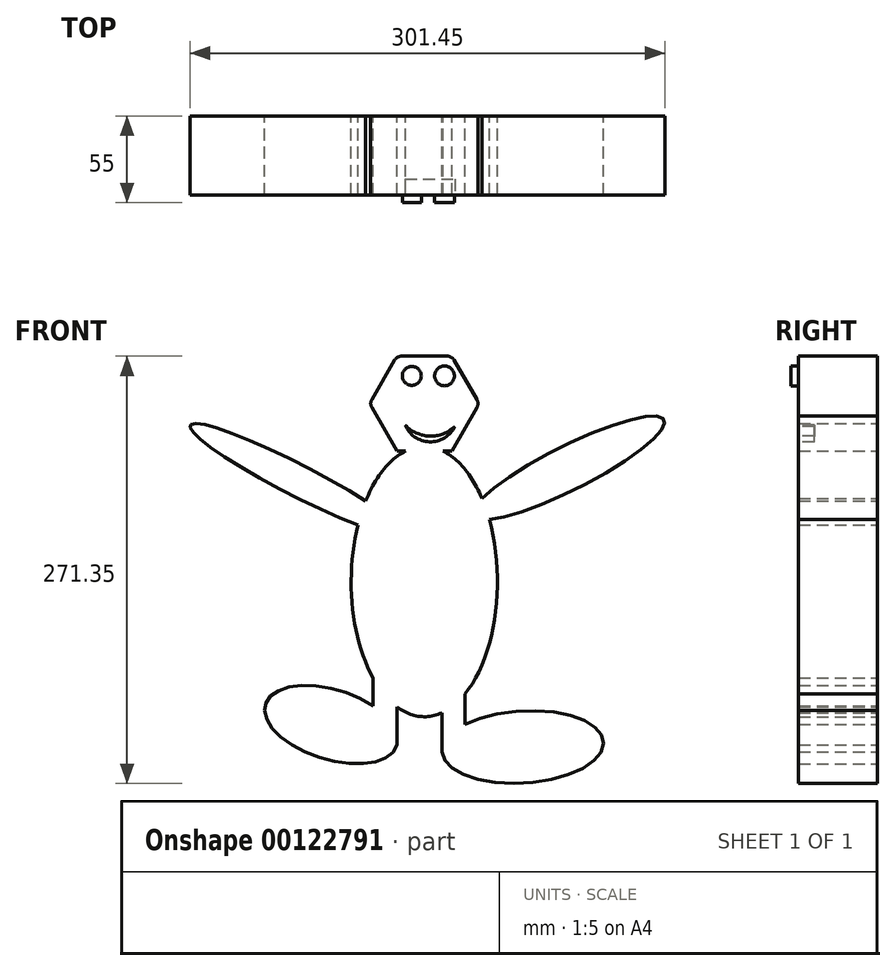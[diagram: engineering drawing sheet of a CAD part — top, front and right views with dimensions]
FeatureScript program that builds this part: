
annotation { "Feature Type Name" : "Feature", "Feature Type Description" : "" }
export const myFeature = defineFeature(function(context is Context, id is Id, definition is map)
    precondition{}
    {
        {
            var Q0;
            Q0=qCreatedBy(makeId("Front.planeOp"),FACE);
            var sketch = newSketch(context, id + "F0", { "sketchPlane" : qUnion([Q0])});
            skCircle(sketch, "E0.cCircle", {"center": v(0, 0) * mm, "radius": 30.16 * mm, "construction": true});
            skLineSegment(sketch, "E0.0", {"start": v(-17.41, 30.16) * mm, "end": v(17.41, 30.16) * mm});
            skLineSegment(sketch, "E0.1", {"start": v(17.41, 30.16) * mm, "end": v(34.83, 0) * mm});
            skLineSegment(sketch, "E0.2", {"start": v(34.83, 0) * mm, "end": v(17.41, -30.16) * mm});
            skLineSegment(sketch, "E0.3", {"start": v(17.41, -30.16) * mm, "end": v(-17.41, -30.16) * mm});
            skLineSegment(sketch, "E0.4", {"start": v(-17.41, -30.16) * mm, "end": v(-34.83, 0) * mm});
            skLineSegment(sketch, "E0.5", {"start": v(-34.83, 0) * mm, "end": v(-17.41, 30.16) * mm});
            skPoint(sketch, "E0.0.midPoint", {"position": v(0, 30.16) * mm});
            skSolve(sketch);
        }
        {
            var Q0;
            Q0=makeQuery(id+"F0.imprint","IMPRINT",FACE,{"disambiguationData":[TD([[makeQuery(id+"F0.imprint","IMPRINT",EDGE,{"derivedFrom":sQuery(id+"F0.wireOp",EDGE,"E0.0")}),-1.0]])]});
            extrude(context, id + "F1", {"entities" : qUnion([Q0]), "depth" : 50 * mm});
        }
        {
            var Q0;
            Q0=makeQuery(id+"F1.opExtrude","CAP_FACE",FACE,{"disambiguationData":[OSD([sQuery(id+"F0.wireOp",EDGE,"E0.0"),sQuery(id+"F0.wireOp",EDGE,"E0.1"),sQuery(id+"F0.wireOp",EDGE,"E0.2"),sQuery(id+"F0.wireOp",EDGE,"E0.3"),sQuery(id+"F0.wireOp",EDGE,"E0.4"),sQuery(id+"F0.wireOp",EDGE,"E0.5")])],"isStart":false});
            var sketch = newSketch(context, id + "F2", { "sketchPlane" : qUnion([Q0])});
            skCircle(sketch, "E1", {"center": v(12.81, 17.63) * mm, "radius": 6.28 * mm});
            skCircle(sketch, "E2", {"center": v(-7.97, 17.63) * mm, "radius": 6.02 * mm});
            skArc(sketch, "E3", {"start": v(-12.24, -13.47) * mm, "mid": v(3.23, -24.2) * mm, "end": v(19.33, -14.44) * mm});
            skArc(sketch, "E4", {"start": v(-12.24, -13.47) * mm, "mid": v(3.34, -20.6) * mm, "end": v(19.33, -14.44) * mm});
            skSolve(sketch);
        }
        {
            var Q0;
            Q0=makeQuery(id+"F2.imprint","IMPRINT",FACE,{"disambiguationData":[TD([[makeQuery(id+"F2.imprint","IMPRINT",EDGE,{"derivedFrom":sQuery(id+"F2.wireOp",EDGE,"E2")}),1.0]])]});
            var Q1;
            Q1=makeQuery(id+"F2.imprint","IMPRINT",FACE,{"disambiguationData":[TD([[makeQuery(id+"F2.imprint","IMPRINT",EDGE,{"derivedFrom":sQuery(id+"F2.wireOp",EDGE,"E1")}),1.0]])]});
            extrude(context, id + "F3", {"entities" : qUnion([Q0, Q1]), "operationType" : NewBodyOperationType.ADD, "depth" : 5 * mm});
        }
        {
            var Q0;
            Q0=makeQuery(id+"F2.imprint","IMPRINT",FACE,{"disambiguationData":[TD([[makeQuery(id+"F2.imprint","IMPRINT",EDGE,{"derivedFrom":sQuery(id+"F2.wireOp",EDGE,"E3")}),1.0]])]});
            extrude(context, id + "F4", {"entities" : qUnion([Q0]), "operationType" : NewBodyOperationType.REMOVE, "oppositeDirection" : true, "depth" : 10 * mm});
        }
        {
            var Q0;
            Q0=makeQuery(id+"F1.opExtrude","SWEPT_EDGE",EDGE,{"disambiguationData":[OSD([sQuery(id+"F0.wireOp",EDGE,"E0.0"),sQuery(id+"F0.wireOp",EDGE,"E0.1")])]});
            var Q1;
            Q1=makeQuery(id+"F1.opExtrude","SWEPT_EDGE",EDGE,{"disambiguationData":[OSD([sQuery(id+"F0.wireOp",EDGE,"E0.0"),sQuery(id+"F0.wireOp",EDGE,"E0.5")])]});
            var Q2;
            Q2=makeQuery(id+"F1.opExtrude","SWEPT_EDGE",EDGE,{"disambiguationData":[OSD([sQuery(id+"F0.wireOp",EDGE,"E0.1"),sQuery(id+"F0.wireOp",EDGE,"E0.2")])]});
            var Q3;
            Q3=makeQuery(id+"F1.opExtrude","SWEPT_EDGE",EDGE,{"disambiguationData":[OSD([sQuery(id+"F0.wireOp",EDGE,"E0.4"),sQuery(id+"F0.wireOp",EDGE,"E0.5")])]});
            fillet(context, id + "F5", {"entities" : qUnion([Q0, Q1, Q2, Q3]), "radius" : 5 * mm, "tangentPropagation" : true, "allowEdgeOverflow" : false});
        }
        {
            var Q0;
            Q0=qCreatedBy(makeId("Front.planeOp"),FACE);
            var sketch = newSketch(context, id + "F6", { "sketchPlane" : qUnion([Q0])});
            skEllipse(sketch, "E5", {"center": v(0, -113.06) * mm, "majorRadius": 85.77 * mm, "minorRadius": 46.48 * mm, "majorAxis": v(0, 1)});
            skLineSegment(sketch, "E6.bottom", {"start": v(25.73, -221.24) * mm, "end": v(11.2, -221.24) * mm});
            skLineSegment(sketch, "E6.top", {"start": v(25.73, -181.67) * mm, "end": v(11.2, -181.67) * mm});
            skLineSegment(sketch, "E6.left", {"start": v(25.73, -221.24) * mm, "end": v(25.73, -181.67) * mm});
            skLineSegment(sketch, "E6.right", {"start": v(11.2, -221.24) * mm, "end": v(11.2, -181.67) * mm});
            skLineSegment(sketch, "E7.bottom", {"start": v(-32.66, -216.9) * mm, "end": v(-17.43, -216.9) * mm});
            skLineSegment(sketch, "E7.top", {"start": v(-32.66, -169.58) * mm, "end": v(-17.43, -169.58) * mm});
            skLineSegment(sketch, "E7.left", {"start": v(-32.66, -216.9) * mm, "end": v(-32.66, -169.58) * mm});
            skLineSegment(sketch, "E7.right", {"start": v(-17.43, -216.9) * mm, "end": v(-17.43, -169.58) * mm});
            skEllipse(sketch, "E8", {"center": v(62.55, -218.08) * mm, "majorRadius": 51.44 * mm, "minorRadius": 22.94 * mm, "majorAxis": v(-1, -0.06)});
            skEllipse(sketch, "E9", {"center": v(-59.15, -203.88) * mm, "majorRadius": 43.7 * mm, "minorRadius": 22.25 * mm, "majorAxis": v(0.95, -0.3)});
            skEllipse(sketch, "E10", {"center": v(91.5, -40.9) * mm, "majorRadius": 68.1 * mm, "minorRadius": 13.96 * mm, "majorAxis": v(-0.9, -0.45)});
            skEllipse(sketch, "E11", {"center": v(-81.37, -48.27) * mm, "majorRadius": 75.6 * mm, "minorRadius": 10.05 * mm, "majorAxis": v(0.89, -0.46)});
            skSolve(sketch);
        }
        {
            var Q0;
            {var subQ0=sQuery(id+"F6.wireOp",EDGE,"E10");var subQ1=sQuery(id+"F6.wireOp",EDGE,"E5");var subQ2=makeQuery(id+"F6.imprint","INTERSECT",VERTEX,{"disambiguationData":[OD(0.0)],"derivedFrom":[subQ1,subQ0]});Q0=makeQuery(id+"F6.imprint","IMPRINT",FACE,{"disambiguationData":[TD([[makeQuery(id+"F6.imprint","IMPRINT",EDGE,{"disambiguationData":[TD([[subQ2,-1.0]])],"derivedFrom":subQ1}),-1.0]])]});}
            var Q1;
            {var subQ0=sQuery(id+"F6.wireOp",EDGE,"E11");var subQ1=sQuery(id+"F6.wireOp",EDGE,"E5");var subQ2=makeQuery(id+"F6.imprint","INTERSECT",VERTEX,{"disambiguationData":[OD(0.0)],"derivedFrom":[subQ1,subQ0]});Q1=makeQuery(id+"F6.imprint","IMPRINT",FACE,{"disambiguationData":[TD([[makeQuery(id+"F6.imprint","IMPRINT",EDGE,{"disambiguationData":[TD([[subQ2,1.0]])],"derivedFrom":subQ1}),-1.0]])]});}
            var Q2;
            {var subQ7=sQuery(id+"F6.wireOp",EDGE,"E6.top");Q2=makeQuery(id+"F6.imprint","IMPRINT",FACE,{"disambiguationData":[TD([[makeQuery(id+"F6.imprint","IMPRINT",EDGE,{"derivedFrom":subQ7}),-1.0]])]});}
            var Q3;
            {var subQ0=sQuery(id+"F6.wireOp",EDGE,"E10");var subQ1=sQuery(id+"F6.wireOp",EDGE,"E5");var subQ2=makeQuery(id+"F6.imprint","INTERSECT",VERTEX,{"disambiguationData":[OD(0.0)],"derivedFrom":[subQ1,subQ0]});Q3=makeQuery(id+"F6.imprint","IMPRINT",FACE,{"disambiguationData":[TD([[makeQuery(id+"F6.imprint","IMPRINT",EDGE,{"disambiguationData":[TD([[subQ2,-1.0]])],"derivedFrom":subQ1}),1.0]])]});}
            var Q4;
            {var subQ0=sQuery(id+"F6.wireOp",EDGE,"E11");var subQ1=sQuery(id+"F6.wireOp",EDGE,"E5");var subQ2=makeQuery(id+"F6.imprint","INTERSECT",VERTEX,{"disambiguationData":[OD(0.0)],"derivedFrom":[subQ1,subQ0]});Q4=makeQuery(id+"F6.imprint","IMPRINT",FACE,{"disambiguationData":[TD([[makeQuery(id+"F6.imprint","IMPRINT",EDGE,{"disambiguationData":[TD([[subQ2,1.0]])],"derivedFrom":subQ1}),1.0]])]});}
            var Q5;
            {var subQ5=sQuery(id+"F6.wireOp",EDGE,"E7.top");Q5=makeQuery(id+"F6.imprint","IMPRINT",FACE,{"disambiguationData":[TD([[makeQuery(id+"F6.imprint","IMPRINT",EDGE,{"derivedFrom":subQ5}),-1.0]])]});}
            var Q6;
            {var subQ0=sQuery(id+"F6.wireOp",EDGE,"E7.left");var subQ1=sQuery(id+"F6.wireOp",EDGE,"E5");var subQ2=makeQuery(id+"F6.imprint","INTERSECT",VERTEX,{"derivedFrom":[subQ1,subQ0]});Q6=makeQuery(id+"F6.imprint","IMPRINT",FACE,{"disambiguationData":[TD([[makeQuery(id+"F6.imprint","IMPRINT",EDGE,{"disambiguationData":[TD([[subQ2,-1.0]])],"derivedFrom":subQ1}),-1.0]])]});}
            var Q7;
            {var subQ0=sQuery(id+"F6.wireOp",EDGE,"E7.bottom");Q7=makeQuery(id+"F6.imprint","IMPRINT",FACE,{"disambiguationData":[TD([[makeQuery(id+"F6.imprint","IMPRINT",EDGE,{"derivedFrom":subQ0}),1.0]])]});}
            var Q8;
            {var subQ0=sQuery(id+"F6.wireOp",EDGE,"E7.bottom");Q8=makeQuery(id+"F6.imprint","IMPRINT",FACE,{"disambiguationData":[TD([[makeQuery(id+"F6.imprint","IMPRINT",EDGE,{"derivedFrom":subQ0}),-1.0]])]});}
            var Q9;
            {var subQ5=sQuery(id+"F6.wireOp",EDGE,"E6.top");Q9=makeQuery(id+"F6.imprint","IMPRINT",FACE,{"disambiguationData":[TD([[makeQuery(id+"F6.imprint","IMPRINT",EDGE,{"derivedFrom":subQ5}),1.0]])]});}
            var Q10;
            {var subQ0=sQuery(id+"F6.wireOp",EDGE,"E6.right");var subQ1=sQuery(id+"F6.wireOp",EDGE,"E5");var subQ2=makeQuery(id+"F6.imprint","INTERSECT",VERTEX,{"derivedFrom":[subQ1,subQ0]});Q10=makeQuery(id+"F6.imprint","IMPRINT",FACE,{"disambiguationData":[TD([[makeQuery(id+"F6.imprint","IMPRINT",EDGE,{"disambiguationData":[TD([[subQ2,-1.0]])],"derivedFrom":subQ1}),-1.0]])]});}
            var Q11;
            {var subQ0=sQuery(id+"F6.wireOp",EDGE,"E6.bottom");Q11=makeQuery(id+"F6.imprint","IMPRINT",FACE,{"disambiguationData":[TD([[makeQuery(id+"F6.imprint","IMPRINT",EDGE,{"derivedFrom":subQ0}),-1.0]])]});}
            var Q12;
            {var subQ0=sQuery(id+"F6.wireOp",EDGE,"E6.bottom");Q12=makeQuery(id+"F6.imprint","IMPRINT",FACE,{"disambiguationData":[TD([[makeQuery(id+"F6.imprint","IMPRINT",EDGE,{"derivedFrom":subQ0}),1.0]])]});}
            extrude(context, id + "F7", {"entities" : qUnion([Q0, Q1, Q2, Q3, Q4, Q5, Q6, Q7, Q8, Q9, Q10, Q11, Q12]), "operationType" : NewBodyOperationType.ADD, "depth" : 50 * mm});
        }
    });
